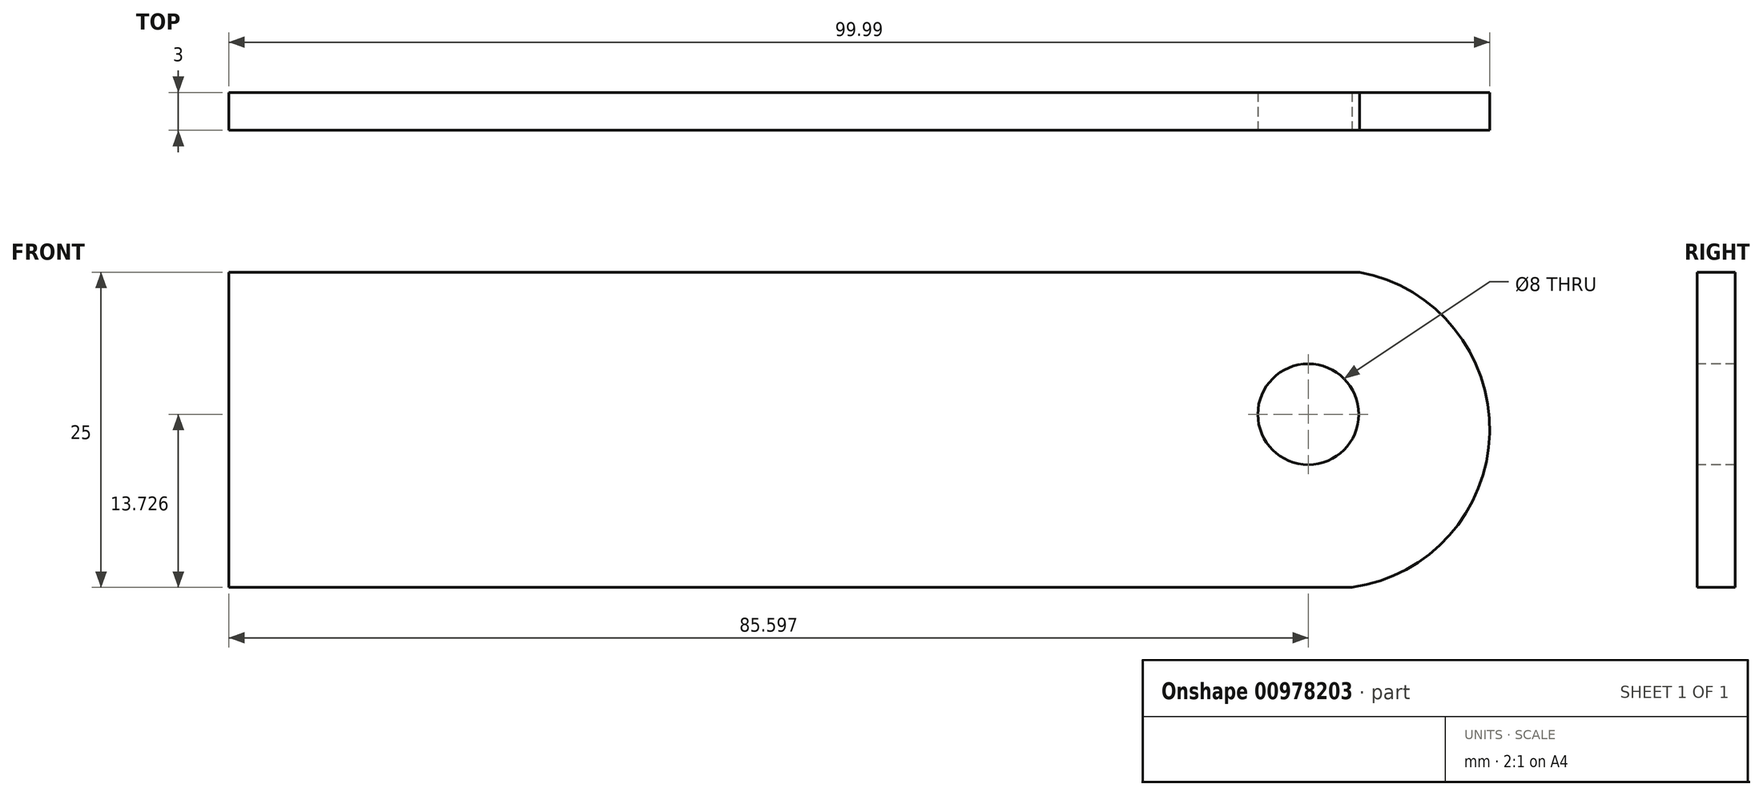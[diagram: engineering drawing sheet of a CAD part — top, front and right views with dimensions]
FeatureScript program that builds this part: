
annotation { "Feature Type Name" : "Feature", "Feature Type Description" : "" }
export const myFeature = defineFeature(function(context is Context, id is Id, definition is map)
    precondition{}
    {
        {
            var Q0;
            Q0=qCreatedBy(makeId("Front.planeOp"),FACE);
            var sketch = newSketch(context, id + "F0", { "sketchPlane" : qUnion([Q0])});
            skLineSegment(sketch, "E0.bottom", {"start": v(4.65, -40.82) * mm, "end": v(-95.35, -40.82) * mm});
            skLineSegment(sketch, "E0.top", {"start": v(4.65, -65.82) * mm, "end": v(-95.35, -65.82) * mm});
            skLineSegment(sketch, "E0.left", {"start": v(4.65, -40.82) * mm, "end": v(4.65, -65.82) * mm});
            skLineSegment(sketch, "E0.right", {"start": v(-95.35, -40.82) * mm, "end": v(-95.35, -65.82) * mm});
            skPoint(sketch, "E0.middle", {"position": v(-45.35, -53.32) * mm});
            skSolve(sketch);
        }
        {
            var Q0;
            Q0=makeQuery(id+"F0.imprint","IMPRINT",FACE,{"disambiguationData":[TD([[makeQuery(id+"F0.imprint","IMPRINT",EDGE,{"derivedFrom":sQuery(id+"F0.wireOp",EDGE,"E0.bottom")}),1.0]])]});
            extrude(context, id + "F1", {"entities" : qUnion([Q0]), "depth" : 3 * mm, "offsetDistance" : 25 * mm});
        }
        {
            var Q0;
            Q0=makeQuery(id+"F1.opExtrude","CAP_FACE",FACE,{"disambiguationData":[OSD([sQuery(id+"F0.wireOp",EDGE,"E0.bottom"),sQuery(id+"F0.wireOp",EDGE,"E0.top"),sQuery(id+"F0.wireOp",EDGE,"E0.left"),sQuery(id+"F0.wireOp",EDGE,"E0.right")])],"isStart":false});
            var sketch = newSketch(context, id + "F2", { "sketchPlane" : qUnion([Q0])});
            skArc(sketch, "E1", {"start": v(-9.78, -65.82) * mm, "mid": v(4.63, -52.97) * mm, "end": v(-10.39, -40.82) * mm});
            skSolve(sketch);
        }
        {
            var Q0;
            {var subQ5=makeQuery(id+"F1.opExtrude","CAP_EDGE",EDGE,{"disambiguationData":[OSD([sQuery(id+"F0.wireOp",EDGE,"E0.left")])],"isStart":false});Q0=makeQuery(id+"F2.imprint","IMPRINT",FACE,{"disambiguationData":[TD([[makeQuery(id+"F2.imprint","IMPRINT",EDGE,{"derivedFrom":subQ5}),-1.0]])]});}
            extrude(context, id + "F3", {"entities" : qUnion([Q0]), "operationType" : NewBodyOperationType.REMOVE, "endBound" : BoundingType.THROUGH_ALL, "oppositeDirection" : true, "depth" : 25 * mm, "offsetDistance" : 25 * mm});
        }
        {
            var Q0;
            Q0=makeQuery(id+"F1.opExtrude","CAP_FACE",FACE,{"disambiguationData":[OSD([sQuery(id+"F0.wireOp",EDGE,"E0.bottom"),sQuery(id+"F0.wireOp",EDGE,"E0.top"),sQuery(id+"F0.wireOp",EDGE,"E0.left"),sQuery(id+"F0.wireOp",EDGE,"E0.right")])],"isStart":false});
            var sketch = newSketch(context, id + "F4", { "sketchPlane" : qUnion([Q0])});
            skSolve(sketch);
        }
        {
            var Q0;
            Q0=makeQuery(id+"F4.imprint","IMPRINT",FACE,{"disambiguationData":[TD([[makeQuery(id+"F4.imprint","IMPRINT",EDGE,{"derivedFrom":makeQuery(id+"F1.opExtrude","CAP_EDGE",EDGE,{"disambiguationData":[OSD([sQuery(id+"F0.wireOp",EDGE,"E0.right")])],"isStart":false})}),1.0]])]});
            var sketch = newSketch(context, id + "F5", { "sketchPlane" : qUnion([Q0])});
            skCircle(sketch, "E2", {"center": v(-9.75, -52.1) * mm, "radius": 4 * mm});
            skSolve(sketch);
        }
        {
            var Q0;
            Q0 = qSketchRegion(id + "F5", true);
            extrude(context, id + "F6", {"entities" : qUnion([Q0]), "operationType" : NewBodyOperationType.ADD, "depth" : 25 * mm, "offsetDistance" : 25 * mm});
        }
        {
            var Q0;
            Q0=makeQuery(id+"F6.opExtrude","CAP_FACE",FACE,{"disambiguationData":[OSD([sQuery(id+"F5.wireOp",EDGE,"E2")])],"isStart":false});
            extrude(context, id + "F7", {"entities" : qUnion([Q0]), "operationType" : NewBodyOperationType.REMOVE, "endBound" : BoundingType.THROUGH_ALL, "oppositeDirection" : true, "depth" : 25 * mm, "offsetDistance" : 25 * mm});
        }
    });
